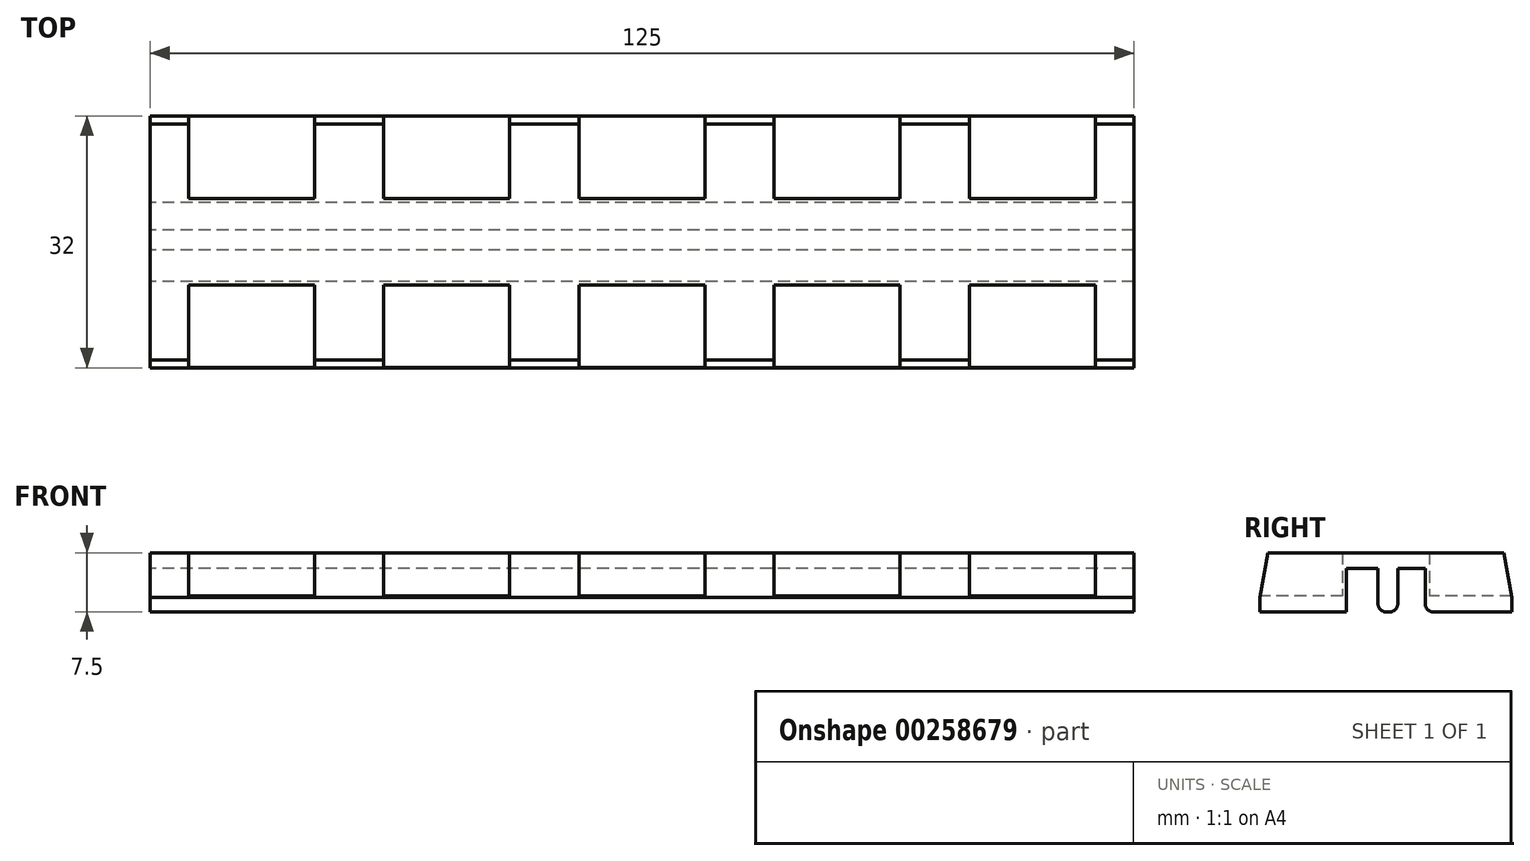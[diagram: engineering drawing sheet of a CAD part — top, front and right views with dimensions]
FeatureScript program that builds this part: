
annotation { "Feature Type Name" : "Feature", "Feature Type Description" : "" }
export const myFeature = defineFeature(function(context is Context, id is Id, definition is map)
    precondition{}
    {
        {
            var Q0;
            Q0=qCreatedBy(makeId("Top.planeOp"),FACE);
            var sketch = newSketch(context, id + "F0", { "sketchPlane" : qUnion([Q0])});
            skLineSegment(sketch, "E0.bottom", {"start": v(62.5, -16.5) * mm, "end": v(57.6, -16.5) * mm});
            skLineSegment(sketch, "E0.top", {"start": v(62.5, 15.5) * mm, "end": v(57.6, 15.5) * mm});
            skLineSegment(sketch, "E0.left", {"start": v(62.5, -16.5) * mm, "end": v(62.5, 15.5) * mm});
            skLineSegment(sketch, "E0.right", {"start": v(-62.5, -16.5) * mm, "end": v(-62.5, 15.5) * mm});
            skPoint(sketch, "E0.middle", {"position": v(0, 0) * mm});
            skLineSegment(sketch, "E1.left", {"start": v(-41.6, 15.5) * mm, "end": v(-41.6, 5) * mm});
            skLineSegment(sketch, "E1.right", {"start": v(-57.6, 15.5) * mm, "end": v(-57.6, 5) * mm});
            skPoint(sketch, "E1.middle", {"position": v(-49.6, -0.5) * mm});
            skLineSegment(sketch, "E2.bottom", {"start": v(-41.6, -6) * mm, "end": v(-57.6, -6) * mm});
            skLineSegment(sketch, "E2.top", {"start": v(-41.6, 5) * mm, "end": v(-57.6, 5) * mm});
            skLineSegment(sketch, "E3.trimOffspring", {"start": v(-41.6, -6) * mm, "end": v(-41.6, -16.5) * mm});
            skLineSegment(sketch, "E4.trimOffspring", {"start": v(-57.6, -6) * mm, "end": v(-57.6, -16.5) * mm});
            skLineSegment(sketch, "E5", {"start": v(-83.3, 5) * mm, "end": v(-62.43, 5) * mm, "construction": true});
            skLineSegment(sketch, "E6", {"start": v(-82.83, -6) * mm, "end": v(-62.43, -6) * mm, "construction": true});
            skLineSegment(sketch, "E7.top", {"start": v(-32.8, 5) * mm, "end": v(-16.8, 5) * mm});
            skLineSegment(sketch, "E7.left", {"start": v(-32.8, 15.5) * mm, "end": v(-32.8, 5) * mm});
            skLineSegment(sketch, "E7.right", {"start": v(-16.8, 15.5) * mm, "end": v(-16.8, 5) * mm});
            skLineSegment(sketch, "E8.top", {"start": v(-8, 5) * mm, "end": v(8, 5) * mm});
            skLineSegment(sketch, "E8.left", {"start": v(-8, 15.5) * mm, "end": v(-8, 5) * mm});
            skLineSegment(sketch, "E8.right", {"start": v(8, 15.5) * mm, "end": v(8, 5) * mm});
            skLineSegment(sketch, "E9.top", {"start": v(16.8, 5) * mm, "end": v(32.8, 5) * mm});
            skLineSegment(sketch, "E9.left", {"start": v(16.8, 15.5) * mm, "end": v(16.8, 5) * mm});
            skLineSegment(sketch, "E9.right", {"start": v(32.8, 15.5) * mm, "end": v(32.8, 5) * mm});
            skLineSegment(sketch, "E10.top", {"start": v(41.6, 5) * mm, "end": v(57.6, 5) * mm});
            skLineSegment(sketch, "E10.left", {"start": v(41.6, 15.5) * mm, "end": v(41.6, 5) * mm});
            skLineSegment(sketch, "E10.right", {"start": v(57.6, 15.5) * mm, "end": v(57.6, 5) * mm});
            skLineSegment(sketch, "E11.bottom", {"start": v(-32.8, -6) * mm, "end": v(-16.8, -6) * mm});
            skLineSegment(sketch, "E11.left", {"start": v(-32.8, -6) * mm, "end": v(-32.8, -16.5) * mm});
            skLineSegment(sketch, "E11.right", {"start": v(-16.8, -6) * mm, "end": v(-16.8, -16.5) * mm});
            skLineSegment(sketch, "E12.bottom", {"start": v(-8, -6) * mm, "end": v(8, -6) * mm});
            skLineSegment(sketch, "E12.left", {"start": v(-8, -6) * mm, "end": v(-8, -16.5) * mm});
            skLineSegment(sketch, "E12.right", {"start": v(8, -6) * mm, "end": v(8, -16.5) * mm});
            skLineSegment(sketch, "E13.bottom", {"start": v(16.8, -6) * mm, "end": v(32.8, -6) * mm});
            skLineSegment(sketch, "E13.left", {"start": v(16.8, -6) * mm, "end": v(16.8, -16.5) * mm});
            skLineSegment(sketch, "E13.right", {"start": v(32.8, -6) * mm, "end": v(32.8, -16.5) * mm});
            skLineSegment(sketch, "E14.bottom", {"start": v(41.6, -6) * mm, "end": v(57.6, -6) * mm});
            skLineSegment(sketch, "E14.left", {"start": v(41.6, -6) * mm, "end": v(41.6, -16.5) * mm});
            skLineSegment(sketch, "E14.right", {"start": v(57.6, -6) * mm, "end": v(57.6, -16.5) * mm});
            skLineSegment(sketch, "E15.trimOffspring", {"start": v(-57.6, 15.5) * mm, "end": v(-62.5, 15.5) * mm});
            skLineSegment(sketch, "E16.trimOffspring", {"start": v(-32.8, 15.5) * mm, "end": v(-41.6, 15.5) * mm});
            skLineSegment(sketch, "E17.trimOffspring", {"start": v(-8, 15.5) * mm, "end": v(-16.8, 15.5) * mm});
            skLineSegment(sketch, "E18.trimOffspring", {"start": v(16.8, 15.5) * mm, "end": v(8, 15.5) * mm});
            skLineSegment(sketch, "E19.trimOffspring", {"start": v(41.6, 15.5) * mm, "end": v(32.8, 15.5) * mm});
            skLineSegment(sketch, "E20.trimOffspring", {"start": v(41.6, -16.5) * mm, "end": v(32.8, -16.5) * mm});
            skLineSegment(sketch, "E21.trimOffspring", {"start": v(16.8, -16.5) * mm, "end": v(8, -16.5) * mm});
            skLineSegment(sketch, "E22.trimOffspring", {"start": v(-8, -16.5) * mm, "end": v(-16.8, -16.5) * mm});
            skLineSegment(sketch, "E23.trimOffspring", {"start": v(-32.8, -16.5) * mm, "end": v(-41.6, -16.5) * mm});
            skLineSegment(sketch, "E24.trimOffspring", {"start": v(-57.6, -16.5) * mm, "end": v(-62.5, -16.5) * mm});
            skLineSegment(sketch, "E25.trimOffspring", {"start": v(-57.6, -6) * mm, "end": v(66.83, -6) * mm, "construction": true});
            skLineSegment(sketch, "E26.trimOffspring", {"start": v(-57.6, 5) * mm, "end": v(69, 5) * mm, "construction": true});
            skLineSegment(sketch, "E27", {"start": v(-82.84, 15.5) * mm, "end": v(86.7, 15.5) * mm, "construction": true});
            skLineSegment(sketch, "E28", {"start": v(-85.66, -16.5) * mm, "end": v(85.43, -16.5) * mm, "construction": true});
            skSolve(sketch);
        }
        {
            var Q0;
            Q0 = qSketchRegion(id + "F0", true);
            extrude(context, id + "F1", {"entities" : qUnion([Q0]), "depth" : 5.5 * mm});
        }
        {
            var Q0;
            {var subQ0=sQuery(id+"F0.wireOp",EDGE,"E18.trimOffspring");var subQ1=sQuery(id+"F0.wireOp",EDGE,"E16.trimOffspring");var subQ2=sQuery(id+"F0.wireOp",EDGE,"E15.trimOffspring");var subQ3=sQuery(id+"F0.wireOp",EDGE,"E17.trimOffspring");var subQ4=sQuery(id+"F0.wireOp",EDGE,"E10.left");var subQ5=sQuery(id+"F0.wireOp",EDGE,"E9.left");var subQ6=sQuery(id+"F0.wireOp",EDGE,"E8.right");var subQ7=sQuery(id+"F0.wireOp",EDGE,"E8.left");var subQ8=sQuery(id+"F0.wireOp",EDGE,"E9.top");var subQ9=sQuery(id+"F0.wireOp",EDGE,"E9.right");var subQ10=sQuery(id+"F0.wireOp",EDGE,"E10.right");var subQ11=sQuery(id+"F0.wireOp",EDGE,"E10.top");var subQ12=sQuery(id+"F0.wireOp",EDGE,"E1.left");var subQ13=sQuery(id+"F0.wireOp",EDGE,"E7.top");var subQ14=sQuery(id+"F0.wireOp",EDGE,"E0.top");var subQ15=sQuery(id+"F0.wireOp",EDGE,"E8.top");var subQ16=sQuery(id+"F0.wireOp",EDGE,"E0.left");var subQ17=sQuery(id+"F0.wireOp",EDGE,"E2.top");var subQ18=sQuery(id+"F0.wireOp",EDGE,"E1.right");var subQ19=sQuery(id+"F0.wireOp",EDGE,"E7.left");var subQ20=sQuery(id+"F0.wireOp",EDGE,"E0.right");var subQ21=sQuery(id+"F0.wireOp",EDGE,"E7.right");var subQ22=sQuery(id+"F0.wireOp",EDGE,"E19.trimOffspring");Q0=makeQuery(id+"F5.boolean.opBoolean","SPLIT",FACE,{"disambiguationData":[TD([makeQuery(id+"F1.opExtrude","SWEPT_FACE",FACE,{"disambiguationData":[OSD([subQ14])]})])],"derivedFrom":makeQuery(id+"F1.opExtrude","CAP_FACE",FACE,{"disambiguationData":[OSD([sQuery(id+"F0.wireOp",EDGE,"E0.bottom"),subQ14,subQ16,subQ20,subQ12,subQ18,sQuery(id+"F0.wireOp",EDGE,"E2.bottom"),subQ17,sQuery(id+"F0.wireOp",EDGE,"E3.trimOffspring"),sQuery(id+"F0.wireOp",EDGE,"E4.trimOffspring"),subQ13,subQ19,subQ21,subQ15,subQ7,subQ6,subQ8,subQ5,subQ9,subQ11,subQ4,subQ10,sQuery(id+"F0.wireOp",EDGE,"E11.bottom"),sQuery(id+"F0.wireOp",EDGE,"E11.left"),sQuery(id+"F0.wireOp",EDGE,"E11.right"),sQuery(id+"F0.wireOp",EDGE,"E12.bottom"),sQuery(id+"F0.wireOp",EDGE,"E12.left"),sQuery(id+"F0.wireOp",EDGE,"E12.right"),sQuery(id+"F0.wireOp",EDGE,"E13.bottom"),sQuery(id+"F0.wireOp",EDGE,"E13.left"),sQuery(id+"F0.wireOp",EDGE,"E13.right"),sQuery(id+"F0.wireOp",EDGE,"E14.bottom"),sQuery(id+"F0.wireOp",EDGE,"E14.left"),sQuery(id+"F0.wireOp",EDGE,"E14.right"),subQ2,subQ1,subQ3,subQ0,subQ22,sQuery(id+"F0.wireOp",EDGE,"E20.trimOffspring"),sQuery(id+"F0.wireOp",EDGE,"E21.trimOffspring"),sQuery(id+"F0.wireOp",EDGE,"E22.trimOffspring"),sQuery(id+"F0.wireOp",EDGE,"E23.trimOffspring"),sQuery(id+"F0.wireOp",EDGE,"E24.trimOffspring")])],"isStart":true})});}
            var sketch = newSketch(context, id + "F2", { "sketchPlane" : qUnion([Q0])});
            skLineSegment(sketch, "E29.bottom", {"start": v(-62.5, -15.5) * mm, "end": v(62.5, -15.5) * mm});
            skLineSegment(sketch, "E29.top", {"start": v(-62.5, 16.5) * mm, "end": v(62.5, 16.5) * mm});
            skLineSegment(sketch, "E29.left", {"start": v(-62.5, -15.5) * mm, "end": v(-62.5, 16.5) * mm});
            skLineSegment(sketch, "E29.right", {"start": v(62.5, -15.5) * mm, "end": v(62.5, 16.5) * mm});
            skSolve(sketch);
        }
        {
            var Q0;
            Q0 = qSketchRegion(id + "F2", true);
            extrude(context, id + "F3", {"entities" : qUnion([Q0]), "operationType" : NewBodyOperationType.ADD, "depth" : 2 * mm});
        }
        {
            var Q0;
            Q0=makeQuery(id+"F1.opExtrude","SWEPT_FACE",FACE,{"disambiguationData":[OSD([sQuery(id+"F0.wireOp",EDGE,"E0.right")])]});
            var sketch = newSketch(context, id + "F4", { "sketchPlane" : qUnion([Q0])});
            skLineSegment(sketch, "E30.bottom", {"start": v(-4.5, -2) * mm, "end": v(-1, -2) * mm});
            skLineSegment(sketch, "E30.top", {"start": v(-4.5, 3.5) * mm, "end": v(-1, 3.5) * mm});
            skLineSegment(sketch, "E30.left", {"start": v(-4.5, -2) * mm, "end": v(-4.5, 3.5) * mm});
            skLineSegment(sketch, "E30.right", {"start": v(-1, -2) * mm, "end": v(-1, 3.5) * mm});
            skLineSegment(sketch, "E31.bottom", {"start": v(1.5, -2) * mm, "end": v(5.5, -2) * mm});
            skLineSegment(sketch, "E31.top", {"start": v(1.5, 3.5) * mm, "end": v(5.5, 3.5) * mm});
            skLineSegment(sketch, "E31.left", {"start": v(5.5, 3.5) * mm, "end": v(5.5, -2) * mm});
            skLineSegment(sketch, "E31.right", {"start": v(1.5, 3.5) * mm, "end": v(1.5, -2) * mm});
            skSolve(sketch);
        }
        {
            var Q0;
            Q0 = qSketchRegion(id + "F4", true);
            var Q1;
            Q1=makeQuery(id+"F1.opExtrude","SWEPT_FACE",FACE,{"disambiguationData":[OSD([sQuery(id+"F0.wireOp",EDGE,"E0.left")])]});
            extrude(context, id + "F5", {"entities" : qUnion([Q0]), "operationType" : NewBodyOperationType.REMOVE, "endBound" : BoundingType.UP_TO_SURFACE, "oppositeDirection" : true, "endBoundEntityFace" : qUnion([Q1]), "depth" : 25 * mm});
        }
        {
            var Q0;
            Q0=makeQuery(id+"F5.boolean.opBoolean","COPY",EDGE,{"derivedFrom":makeQuery(id+"F5.opExtrude","SWEPT_EDGE",EDGE,{"disambiguationData":[OSD([sQuery(id+"F2.wireOp",EDGE,"E29.left"),sQuery(id+"F4.wireOp",EDGE,"E30.bottom"),sQuery(id+"F4.wireOp",EDGE,"E30.left")])]})});
            var Q1;
            Q1=makeQuery(id+"F5.boolean.opBoolean","COPY",EDGE,{"derivedFrom":makeQuery(id+"F5.opExtrude","SWEPT_EDGE",EDGE,{"disambiguationData":[OSD([sQuery(id+"F2.wireOp",EDGE,"E29.left"),sQuery(id+"F4.wireOp",EDGE,"E30.bottom"),sQuery(id+"F4.wireOp",EDGE,"E30.right")])]})});
            var Q2;
            Q2=makeQuery(id+"F5.boolean.opBoolean","COPY",EDGE,{"derivedFrom":makeQuery(id+"F5.opExtrude","SWEPT_EDGE",EDGE,{"disambiguationData":[OSD([sQuery(id+"F2.wireOp",EDGE,"E29.left"),sQuery(id+"F4.wireOp",EDGE,"E31.bottom"),sQuery(id+"F4.wireOp",EDGE,"E31.left")])]})});
            var Q3;
            Q3=makeQuery(id+"F5.boolean.opBoolean","COPY",EDGE,{"derivedFrom":makeQuery(id+"F5.opExtrude","SWEPT_EDGE",EDGE,{"disambiguationData":[OSD([sQuery(id+"F2.wireOp",EDGE,"E29.left"),sQuery(id+"F4.wireOp",EDGE,"E31.bottom"),sQuery(id+"F4.wireOp",EDGE,"E31.right")])]})});
            fillet(context, id + "F6", {"entities" : qUnion([Q0, Q1, Q2, Q3]), "radius" : 1 * mm, "tangentPropagation" : true, "allowEdgeOverflow" : false});
        }
        {
            var Q0;
            Q0=makeQuery(id+"F1.opExtrude","CAP_EDGE",EDGE,{"disambiguationData":[OSD([sQuery(id+"F0.wireOp",EDGE,"E15.trimOffspring")])],"isStart":false});
            var Q1;
            Q1=makeQuery(id+"F1.opExtrude","CAP_EDGE",EDGE,{"disambiguationData":[OSD([sQuery(id+"F0.wireOp",EDGE,"E23.trimOffspring")])],"isStart":false});
            chamfer(context, id + "F7", {"entities" : qUnion([Q0, Q1]), "chamferType" : ChamferType.OFFSET_ANGLE, "width" : 1 * mm, "oppositeDirection" : false, "angle" : 80 * degree, "tangentPropagation" : true});
        }
    });
